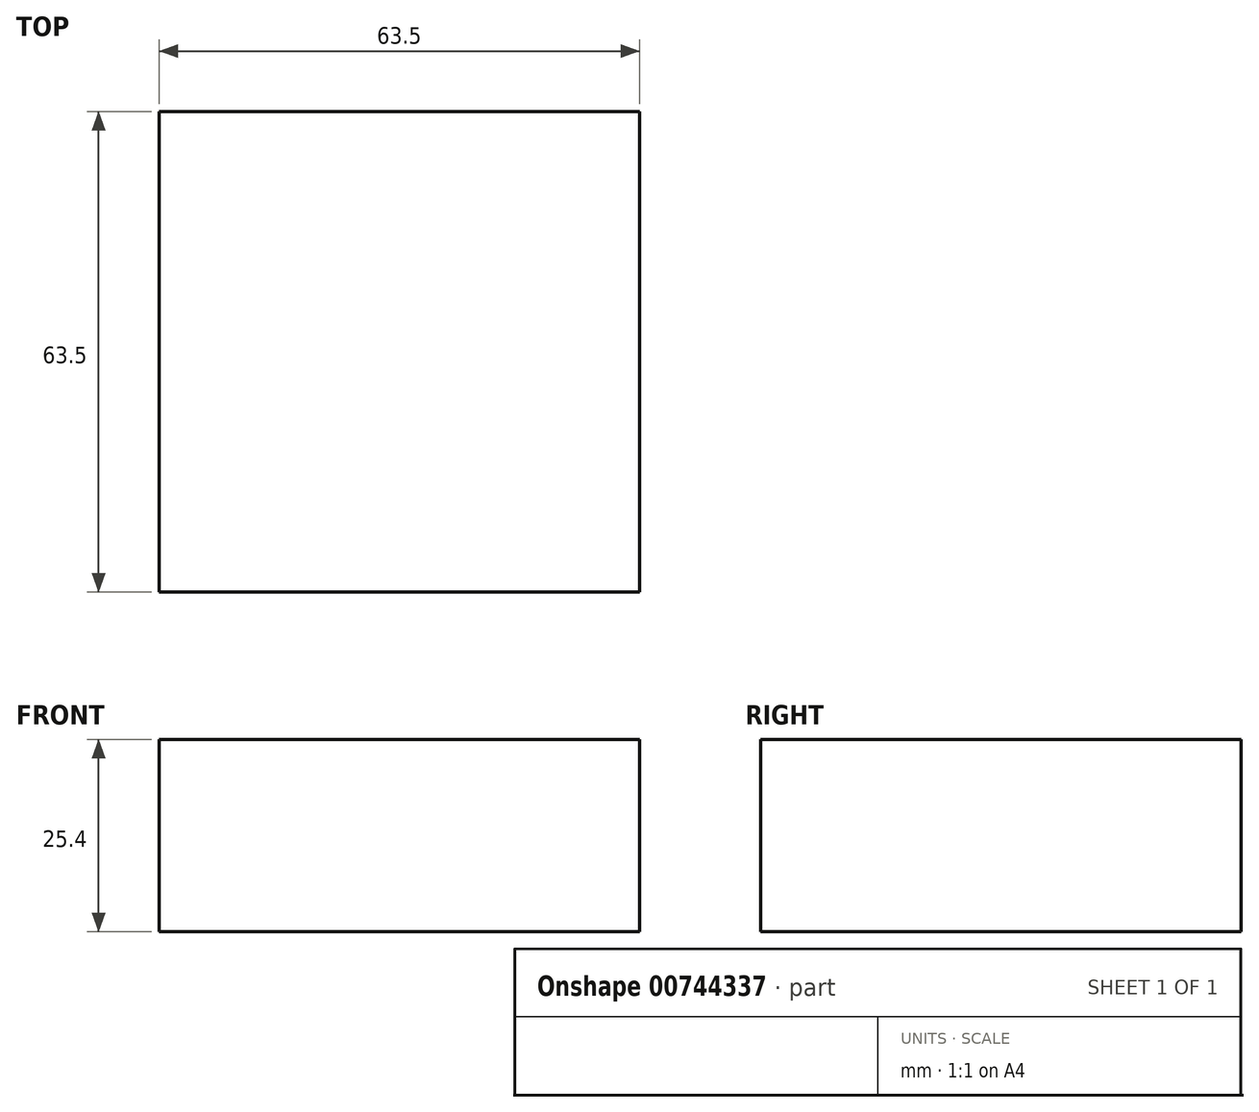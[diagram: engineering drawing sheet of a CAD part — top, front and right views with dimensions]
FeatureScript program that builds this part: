
annotation { "Feature Type Name" : "Feature", "Feature Type Description" : "" }
export const myFeature = defineFeature(function(context is Context, id is Id, definition is map)
    precondition{}
    {
        {
            var Q0;
            Q0=qCreatedBy(makeId("Top.planeOp"),FACE);
            var sketch = newSketch(context, id + "F0", { "sketchPlane" : qUnion([Q0])});
            skLineSegment(sketch, "E0.bottom", {"start": v(0, 0) * mm, "end": v(63.5, 0) * mm});
            skLineSegment(sketch, "E0.top", {"start": v(0, 63.5) * mm, "end": v(63.5, 63.5) * mm});
            skLineSegment(sketch, "E0.left", {"start": v(0, 0) * mm, "end": v(0, 63.5) * mm});
            skLineSegment(sketch, "E0.right", {"start": v(63.5, 0) * mm, "end": v(63.5, 63.5) * mm});
            skSolve(sketch);
        }
        {
            var Q0;
            Q0=makeQuery(id+"F0.imprint","IMPRINT",FACE,{"disambiguationData":[TD([[makeQuery(id+"F0.imprint","IMPRINT",EDGE,{"derivedFrom":sQuery(id+"F0.wireOp",EDGE,"E0.bottom")}),1.0]])]});
            extrude(context, id + "F1", {"entities" : qUnion([Q0]), "depth" : 25.4 * mm, "offsetDistance" : 25.4 * mm});
        }
    });
